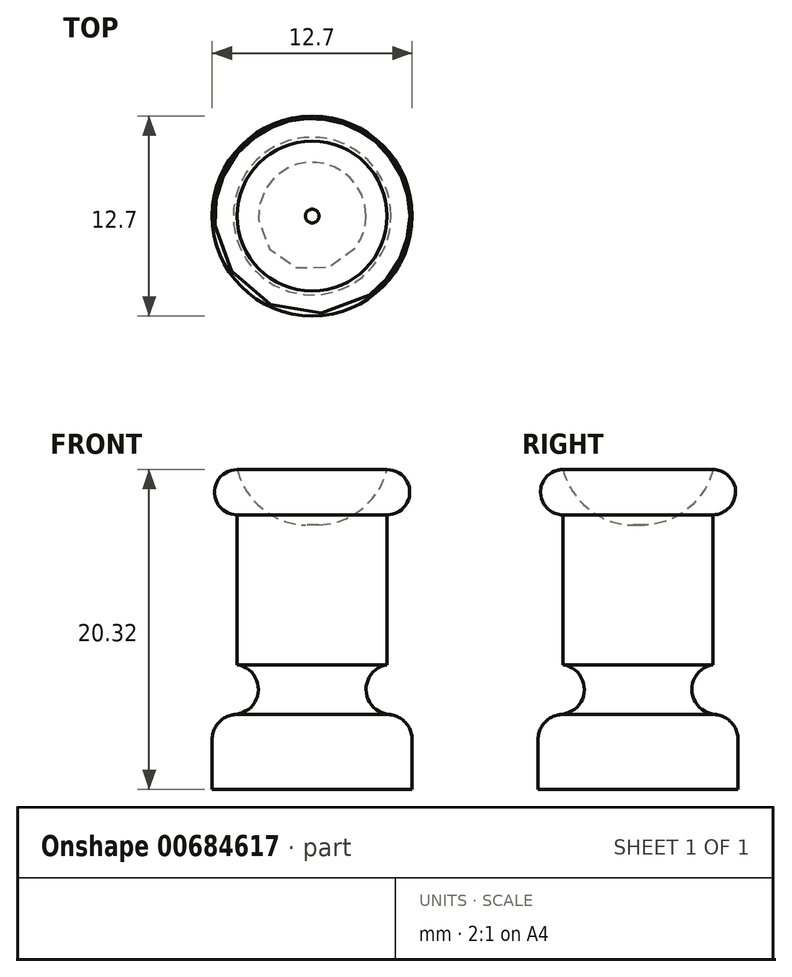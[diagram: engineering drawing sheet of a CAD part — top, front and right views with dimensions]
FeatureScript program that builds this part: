
annotation { "Feature Type Name" : "Feature", "Feature Type Description" : "" }
export const myFeature = defineFeature(function(context is Context, id is Id, definition is map)
    precondition{}
    {
        {
            var Q0;
            Q0=qCreatedBy(makeId("Right.planeOp"),FACE);
            var sketch = newSketch(context, id + "F0", { "sketchPlane" : qUnion([Q0])});
            skLineSegment(sketch, "E0", {"start": v(0, 0) * mm, "end": v(6.35, 0) * mm});
            skLineSegment(sketch, "E1", {"start": v(6.35, 0) * mm, "end": v(6.35, 3.17) * mm});
            skArc(sketch, "E2", {"start": v(6.35, 3.17) * mm, "mid": v(5.89, 4.3) * mm, "end": v(4.76, 4.76) * mm});
            skLineSegment(sketch, "E3", {"start": v(5, 4.76) * mm, "end": v(4.76, 4.76) * mm});
            skArc(sketch, "E4", {"start": v(4.76, 7.92) * mm, "mid": v(3.43, 6.23) * mm, "end": v(5, 4.76) * mm});
            skLineSegment(sketch, "E5", {"start": v(4.76, 7.92) * mm, "end": v(4.76, 17.44) * mm});
            skArc(sketch, "E6", {"start": v(4.76, 17.44) * mm, "mid": v(6.2, 18.88) * mm, "end": v(4.76, 20.32) * mm});
            skArc(sketch, "E7", {"start": v(4.76, 20.32) * mm, "mid": v(3.85, 24.44) * mm, "end": v(0, 26.17) * mm});
            skLineSegment(sketch, "E8", {"start": v(0, 26.17) * mm, "end": v(0, 0) * mm});
            skSolve(sketch);
        }
        {
            var Q0;
            Q0 = qSketchRegion(id + "F0", true);
            var Q1;
            Q1=sQuery(id+"F0.wireOp",EDGE,"E8");
            revolve(context, id + "F1", {"entities" : qUnion([Q0]), "axis" : qUnion([Q1]), "revolveType" : RevolveType.FULL});
        }
    });
